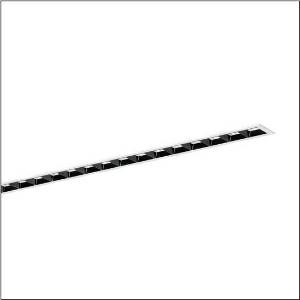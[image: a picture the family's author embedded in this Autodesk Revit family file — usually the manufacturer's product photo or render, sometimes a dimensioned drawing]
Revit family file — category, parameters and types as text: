
# Revit family: silica_r__21_51mx11db35wb_5c76
name_source: partatom
category: Lighting Fixtures
units: mm (PartAtom-declared; Revit-internal decimal feet)

## family parameters
Cut with Voids When Loaded = No
Host = Face
Light Source = No
Part Type = Normal
Room Calculation Point = No
Round Connector Dimension = Use Diameter
Shared = No

## types (1)
- --- (1 x LED, 5400 lm, 34.3 W, 3000K)
    Apparent Load = 34 VA
    CIE Flux Codes = 87 99 100 100 100
    Color Rendering = 80
    Color Temperature = 3000K
    Default Elevation = 1800 mm
    Description = Silica® 21, office luminaire, primary light control with darklight reflector, of PMMA, black, CAT 2 (L<= 3000cd/m²), light emission: direct distribution, primary light characteristic: symmetric, installation type: recessed, LED, rated luminous flux: 5.400lm, luminous efficacy: 157lm/W, light colour: 830, colour temperature: 3000K, with terminal, 3+2-pole, max. 2.5mm², mains connection: 220..240V, AC, 50/60Hz, rated input power: 34.3W, luminaire housing, of aluminium, traffic white (RAL 9016), length: 1.528mm, width: 79mm, height: 53mm, protection rating (complete): IP20, insulation class (complete): insulation class I (protective earthing), certification: CE, permissible operating ambient temperature: 0..+35°C, standard: EN 50419, packaging unit: 1 piece
    Height = 0 mm  [stored 0 ft]
    Lamp = 1 x LED
    Lamp Light Flux = 5400 lm
    Lamp Power = 34.3 W
    Lamp count = 1
    Length = 1527 mm
    Luminous efficacy = 157 lm/W
    Manufacturer = Siteco
    ModVariant = No
    Model = 51MX11DB35WB
    Mounting Place = Ceiling
    Mounting Type = Recessed
    Number of Poles = 1
    OnlyDefault = Yes
    Power Factor = 1
    Product Name = Silica® 21
    Product group = office luminaire | ceiling recessed
    ProductGroupID = 400
    Protection Class = Protection class I
    Protection Degree = IP 20
    RLX_Detail_Level = 1
    RlxData = <blob elided: 42457 chars, md5=03fbcf20>
    Socket = socket
    Standby Power = 0 W
    System Light Flux = 5400 lm
    System Power = 34 W
    Type Comments = factory setting: luminous flux: 100 % | dim-lin: 254 | 393 mA
    Type Image = l_1251632.jpg
    URL = http://relux.com
    VarID = @adj_032597
    Voltage = 0 V
    Weight = 0.00 kg
    Width = 79 mm

note: [stored X ft] marks values corroborated as IEEE doubles in the binary element streams (Revit-internal decimal feet)

## geometry (parser evidence)
native form markers: Blend x4, Sweep x10
no freeform markers — native parametric forms only
